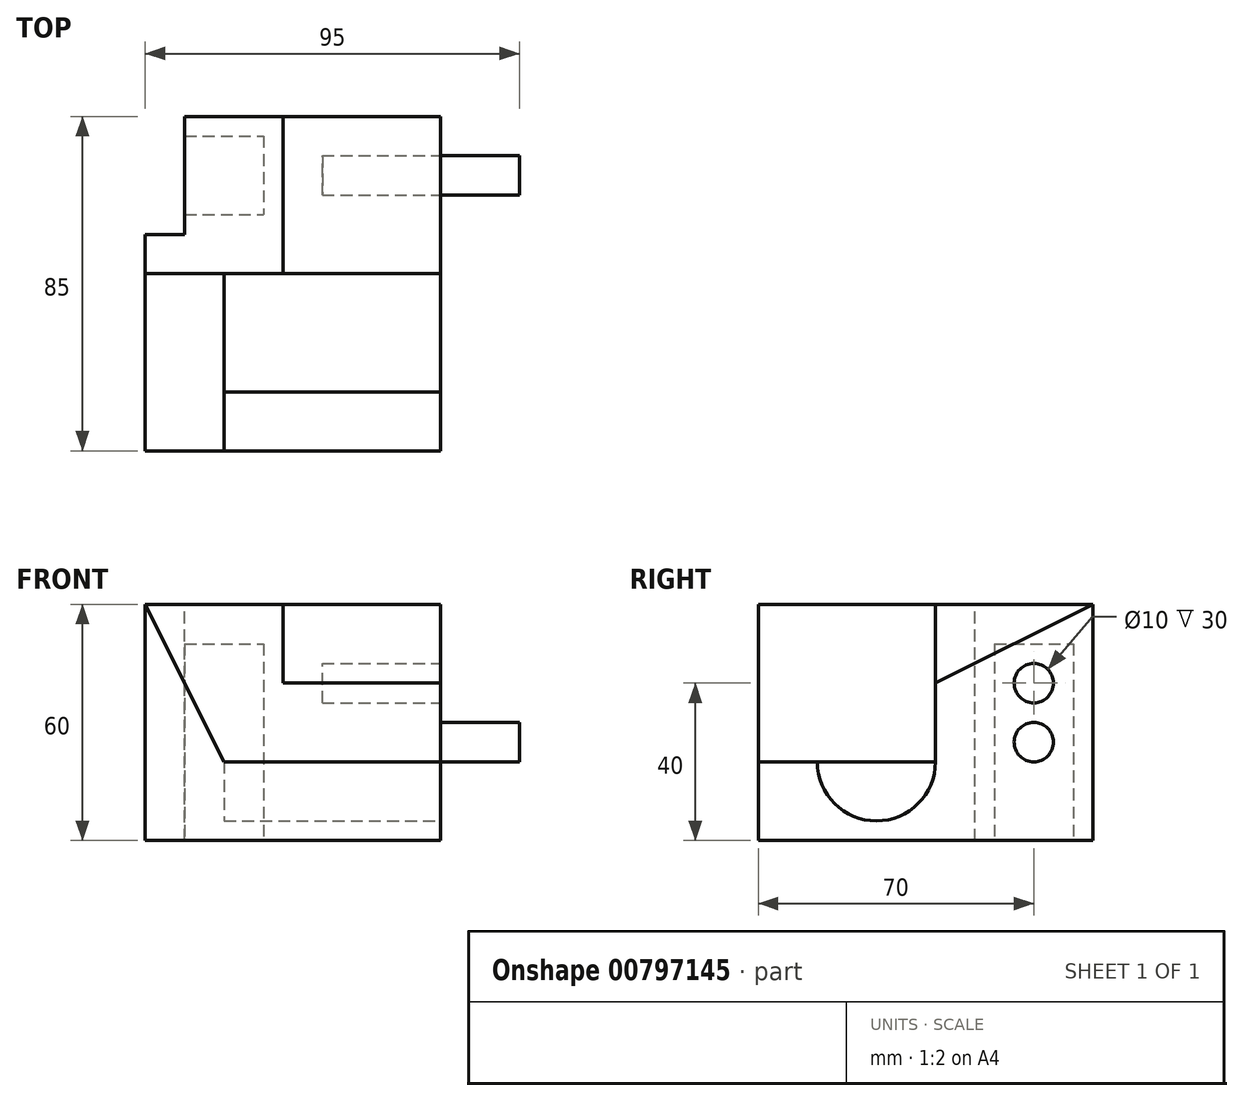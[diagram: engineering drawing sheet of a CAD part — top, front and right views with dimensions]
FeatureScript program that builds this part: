
annotation { "Feature Type Name" : "Feature", "Feature Type Description" : "" }
export const myFeature = defineFeature(function(context is Context, id is Id, definition is map)
    precondition{}
    {
        {
            var Q0;
            Q0=qCreatedBy(makeId("Top.planeOp"),FACE);
            var sketch = newSketch(context, id + "F0", { "sketchPlane" : qUnion([Q0])});
            skLineSegment(sketch, "E0.bottom", {"start": v(75, 85) * mm, "end": v(0, 85) * mm});
            skLineSegment(sketch, "E0.top", {"start": v(75, 0) * mm, "end": v(0, 0) * mm});
            skLineSegment(sketch, "E0.left", {"start": v(75, 85) * mm, "end": v(75, 0) * mm});
            skLineSegment(sketch, "E0.right", {"start": v(0, 85) * mm, "end": v(0, 0) * mm});
            skSolve(sketch);
        }
        {
            var Q0;
            Q0 = qSketchRegion(id + "F0", true);
            extrude(context, id + "F1", {"entities" : qUnion([Q0]), "depth" : 60 * mm, "offsetDistance" : 25 * mm});
        }
        {
            var Q0;
            Q0=makeQuery(id+"F1.opExtrude","SWEPT_FACE",FACE,{"disambiguationData":[OSD([sQuery(id+"F0.wireOp",EDGE,"E0.left")])]});
            var sketch = newSketch(context, id + "F2", { "sketchPlane" : qUnion([Q0])});
            skCircle(sketch, "E1", {"center": v(70, 25) * mm, "radius": 5 * mm});
            skSolve(sketch);
        }
        {
            var Q0;
            Q0 = qSketchRegion(id + "F2", true);
            extrude(context, id + "F3", {"entities" : qUnion([Q0]), "operationType" : NewBodyOperationType.ADD, "depth" : 20 * mm, "offsetDistance" : 25 * mm});
        }
        {
            var Q0;
            Q0=makeQuery(id+"F1.opExtrude","SWEPT_FACE",FACE,{"disambiguationData":[OSD([sQuery(id+"F0.wireOp",EDGE,"E0.left")])]});
            var sketch = newSketch(context, id + "F4", { "sketchPlane" : qUnion([Q0])});
            skCircle(sketch, "E2", {"center": v(70, 40) * mm, "radius": 5 * mm});
            skSolve(sketch);
        }
        {
            var Q0;
            Q0 = qSketchRegion(id + "F4", true);
            extrude(context, id + "F5", {"entities" : qUnion([Q0]), "operationType" : NewBodyOperationType.REMOVE, "oppositeDirection" : true, "depth" : 30 * mm, "offsetDistance" : 25 * mm});
        }
        {
            var Q0;
            Q0=makeQuery(id+"F1.opExtrude","CAP_FACE",FACE,{"disambiguationData":[OSD([sQuery(id+"F0.wireOp",EDGE,"E0.bottom"),sQuery(id+"F0.wireOp",EDGE,"E0.top"),sQuery(id+"F0.wireOp",EDGE,"E0.left"),sQuery(id+"F0.wireOp",EDGE,"E0.right")])],"isStart":false});
            var sketch = newSketch(context, id + "F6", { "sketchPlane" : qUnion([Q0])});
            skLineSegment(sketch, "E3.bottom", {"start": v(10, 55) * mm, "end": v(0, 55) * mm});
            skLineSegment(sketch, "E3.top", {"start": v(10, 85) * mm, "end": v(0, 85) * mm});
            skLineSegment(sketch, "E3.left", {"start": v(10, 55) * mm, "end": v(10, 85) * mm});
            skLineSegment(sketch, "E3.right", {"start": v(0, 55) * mm, "end": v(0, 85) * mm});
            skSolve(sketch);
        }
        {
            var Q0;
            Q0 = qSketchRegion(id + "F6", true);
            extrude(context, id + "F7", {"entities" : qUnion([Q0]), "operationType" : NewBodyOperationType.REMOVE, "endBound" : BoundingType.THROUGH_ALL, "oppositeDirection" : true, "depth" : 25 * mm, "offsetDistance" : 25 * mm});
        }
        {
            var Q0;
            Q0=makeQuery(id+"F1.opExtrude","SWEPT_FACE",FACE,{"disambiguationData":[OSD([sQuery(id+"F0.wireOp",EDGE,"E0.top")])]});
            var sketch = newSketch(context, id + "F8", { "sketchPlane" : qUnion([Q0])});
            skLineSegment(sketch, "E4", {"start": v(0, 60) * mm, "end": v(20, 20) * mm});
            skLineSegment(sketch, "E5", {"start": v(20, 20) * mm, "end": v(20, 60) * mm});
            skLineSegment(sketch, "E6", {"start": v(20, 60) * mm, "end": v(0, 60) * mm});
            skSolve(sketch);
        }
        {
            var Q0;
            Q0 = qSketchRegion(id + "F8", true);
            extrude(context, id + "F9", {"entities" : qUnion([Q0]), "operationType" : NewBodyOperationType.REMOVE, "oppositeDirection" : true, "depth" : 45 * mm, "offsetDistance" : 25 * mm});
        }
        {
            var Q0;
            Q0=makeQuery(id+"F1.opExtrude","SWEPT_FACE",FACE,{"disambiguationData":[OSD([sQuery(id+"F0.wireOp",EDGE,"E0.left")])]});
            var sketch = newSketch(context, id + "F10", { "sketchPlane" : qUnion([Q0])});
            skLineSegment(sketch, "E7", {"start": v(85, 60) * mm, "end": v(45, 40) * mm});
            skLineSegment(sketch, "E8", {"start": v(45, 40) * mm, "end": v(45, 60) * mm});
            skLineSegment(sketch, "E9", {"start": v(45, 60) * mm, "end": v(85, 60) * mm});
            skSolve(sketch);
        }
        {
            var Q0;
            Q0 = qSketchRegion(id + "F10", true);
            extrude(context, id + "F11", {"entities" : qUnion([Q0]), "operationType" : NewBodyOperationType.REMOVE, "oppositeDirection" : true, "depth" : 40 * mm, "offsetDistance" : 25 * mm});
        }
        {
            var Q0;
            Q0=makeQuery(id+"F1.opExtrude","SWEPT_FACE",FACE,{"disambiguationData":[OSD([sQuery(id+"F0.wireOp",EDGE,"E0.left")])]});
            var sketch = newSketch(context, id + "F12", { "sketchPlane" : qUnion([Q0])});
            skLineSegment(sketch, "E10.bottom", {"start": v(45, 60) * mm, "end": v(0, 60) * mm});
            skLineSegment(sketch, "E10.top", {"start": v(45, 20) * mm, "end": v(0, 20) * mm});
            skLineSegment(sketch, "E10.left", {"start": v(45, 60) * mm, "end": v(45, 20) * mm});
            skLineSegment(sketch, "E10.right", {"start": v(0, 60) * mm, "end": v(0, 20) * mm});
            skSolve(sketch);
        }
        {
            var Q0;
            Q0 = qSketchRegion(id + "F12", true);
            extrude(context, id + "F13", {"entities" : qUnion([Q0]), "operationType" : NewBodyOperationType.REMOVE, "oppositeDirection" : true, "depth" : 55 * mm, "offsetDistance" : 25 * mm});
        }
        {
            var Q0;
            Q0=makeQuery(id+"F1.opExtrude","SWEPT_FACE",FACE,{"disambiguationData":[OSD([sQuery(id+"F0.wireOp",EDGE,"E0.left")])]});
            var sketch = newSketch(context, id + "F14", { "sketchPlane" : qUnion([Q0])});
            skCircle(sketch, "E11", {"center": v(30, 20) * mm, "radius": 15 * mm});
            skSolve(sketch);
        }
        {
            var Q0;
            Q0 = qSketchRegion(id + "F14", true);
            var Q1;
            Q1=makeQuery(id+"F13.boolean.opBoolean","MERGE",VERTEX,{"derivedFrom":[makeQuery(id+"F9.boolean.opBoolean","COPY",VERTEX,{"derivedFrom":makeQuery(id+"F9.opExtrude","CAP_VERTEX",VERTEX,{"disambiguationData":[OSD([sQuery(id+"F8.wireOp",EDGE,"E4"),sQuery(id+"F8.wireOp",EDGE,"E5")])],"isStart":true})}),makeQuery(id+"F13.opExtrude","CAP_VERTEX",VERTEX,{"disambiguationData":[OSD([sQuery(id+"F0.wireOp",EDGE,"E0.top"),sQuery(id+"F0.wireOp",EDGE,"E0.left"),sQuery(id+"F12.wireOp",EDGE,"E10.top"),sQuery(id+"F12.wireOp",EDGE,"E10.right")])],"isStart":false})]});
            extrude(context, id + "F15", {"entities" : qUnion([Q0]), "operationType" : NewBodyOperationType.REMOVE, "endBound" : BoundingType.UP_TO_VERTEX, "oppositeDirection" : true, "depth" : 25 * mm, "endBoundEntityVertex" : qUnion([Q1]), "offsetDistance" : 25 * mm});
        }
        {
            var Q0;
            Q0=makeQuery(id+"F1.opExtrude","CAP_FACE",FACE,{"disambiguationData":[OSD([sQuery(id+"F0.wireOp",EDGE,"E0.bottom"),sQuery(id+"F0.wireOp",EDGE,"E0.top"),sQuery(id+"F0.wireOp",EDGE,"E0.left"),sQuery(id+"F0.wireOp",EDGE,"E0.right")])],"isStart":true});
            var sketch = newSketch(context, id + "F16", { "sketchPlane" : qUnion([Q0])});
            skLineSegment(sketch, "E12.bottom", {"start": v(10, -80) * mm, "end": v(30, -80) * mm});
            skLineSegment(sketch, "E12.top", {"start": v(10, -60) * mm, "end": v(30, -60) * mm});
            skLineSegment(sketch, "E12.left", {"start": v(10, -80) * mm, "end": v(10, -60) * mm});
            skLineSegment(sketch, "E12.right", {"start": v(30, -80) * mm, "end": v(30, -60) * mm});
            skSolve(sketch);
        }
        {
            var Q0;
            Q0 = qSketchRegion(id + "F16", true);
            extrude(context, id + "F17", {"entities" : qUnion([Q0]), "operationType" : NewBodyOperationType.REMOVE, "oppositeDirection" : true, "depth" : 50 * mm, "offsetDistance" : 25 * mm});
        }
    });
